# Revit family: Accessory-Soap_Dispenser-KOHLER-Strayt-K-20001T_1
name_source: partatom
category: Specialty Equipment
units: mm (PartAtom-declared; Revit-internal decimal feet)

## family parameters
Cut with Voids When Loaded = No
Host = Face
OmniClass Number = 23.31.25.29.13
OmniClass Title = Hand Soap Dispensers
Part Type = Normal
Room Calculation Point = No
Round Connector Dimension = Use Diameter
Shared = No

## types (2) — shared parameters
ADA Compliant = No
Assembly Code = C1030200
Date Modified = 07/28/2022
Default Elevation = 42"
Finish = Kohler-Metal-S-Polished_Stainless
Height = 16 1/8"
Length = 3 3/4"
Manufacturer = Kohler Co.
Master Format 2014 = 10 28 00
Master Format 2014 Name = Toilet, Bath, and Laundry Accessories
Material = Premium Metal Construction
Product Name = Strayt
URL = http://www.kohler.com.cn
WaterSense Certified = No
Width = 3 7/8"

## per-type parameters (varying)
| type | Description | Model | Product Documentation Link | Product Page URL | Type |
| S-Polished Stainless | Automatic Sensing Foam Soap Dispenser | K-20001T-S | https://files.kohler.com.cn | https://www.kohler.com.cn | 1 |
| B, S-Polished Stainless | Soap Dispenser (Foam) | K-20001T-B-S |  |  | 2 |

## geometry (parser evidence)
native form markers: Sweep x6
no freeform markers — native parametric forms only
